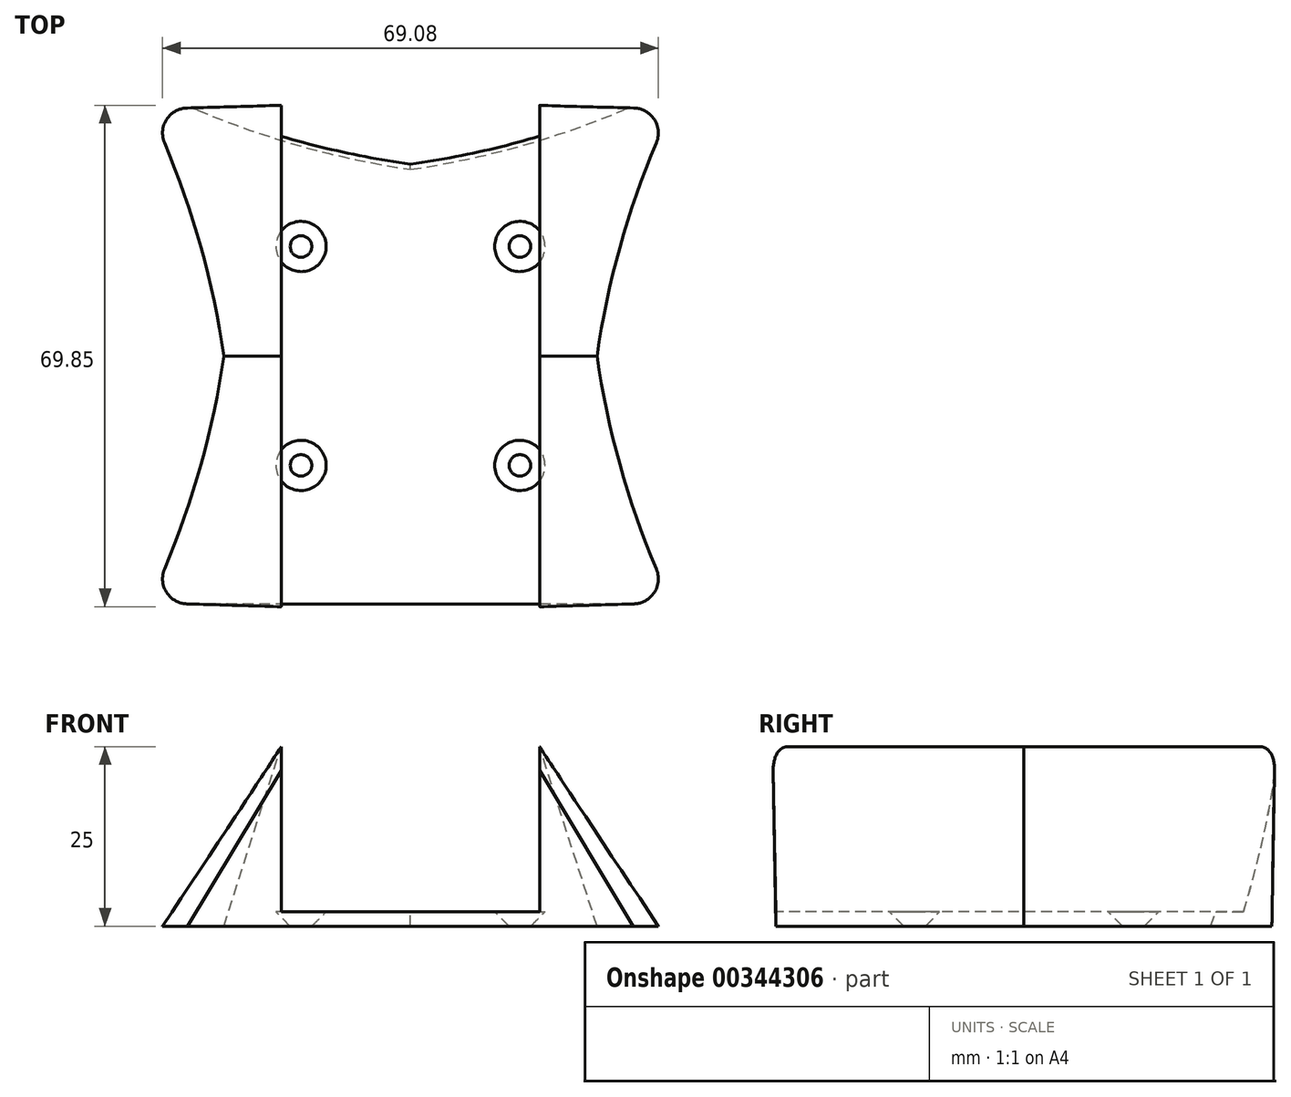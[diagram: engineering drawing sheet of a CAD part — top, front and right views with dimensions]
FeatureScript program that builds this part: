
annotation { "Feature Type Name" : "Feature", "Feature Type Description" : "" }
export const myFeature = defineFeature(function(context is Context, id is Id, definition is map)
    precondition{}
    {
        {
            var Q0;
            Q0=qCreatedBy(makeId("Top.planeOp"),FACE);
            var sketch = newSketch(context, id + "F0", { "sketchPlane" : qUnion([Q0])});
            skLineSegment(sketch, "E0", {"start": v(0, 114.28) * mm, "end": v(0, -108.92) * mm, "construction": true});
            skLineSegment(sketch, "E1", {"start": v(-111.96, 0) * mm, "end": v(120.54, 0) * mm, "construction": true});
            skLineSegment(sketch, "E2", {"start": v(0, 0) * mm, "end": v(98.63, 98.63) * mm, "construction": true});
            skLineSegment(sketch, "E3.0", {"start": v(7.81, 0.88) * mm, "end": v(15.31, 8.38) * mm, "construction": true});
            skCircle(sketch, "E4", {"center": v(15.25, 15.25) * mm, "radius": 1.5 * mm, "construction": true});
            skCircle(sketch, "E5", {"center": v(29.4, 29.4) * mm, "radius": 1.5 * mm, "construction": true});
            skPoint(sketch, "E6", {"position": v(33.52, 33.52) * mm});
            skArc(sketch, "E7", {"start": v(34.27, 29.68) * mm, "mid": v(34.48, 31.71) * mm, "end": v(33.52, 33.52) * mm});
            skLineSegment(sketch, "E8", {"start": v(34.41, 30.1) * mm, "end": v(26, 0) * mm, "construction": true});
            skArc(sketch, "E9", {"start": v(34.27, 29.68) * mm, "mid": v(29.18, 15.1) * mm, "end": v(26, 0) * mm});
            skLineSegment(sketch, "E10", {"start": v(16.13, 0) * mm, "end": v(17.43, 7.28) * mm, "construction": true});
            skArc(sketch, "E11", {"start": v(17.43, 7.28) * mm, "mid": v(16.78, 8.6) * mm, "end": v(15.31, 8.38) * mm, "construction": true});
            skLineSegment(sketch, "E12", {"start": v(18.7, 18.7) * mm, "end": v(19.74, 17.1) * mm, "construction": true});
            skArc(sketch, "E13", {"start": v(19.74, 17.1) * mm, "mid": v(20.87, 16.53) * mm, "end": v(21.92, 17.25) * mm, "construction": true});
            skArc(sketch, "E14", {"start": v(24.57, 22.9) * mm, "mid": v(24.67, 23.66) * mm, "end": v(24.32, 24.32) * mm, "construction": true});
            skLineSegment(sketch, "E15", {"start": v(21.92, 17.25) * mm, "end": v(24.57, 22.9) * mm, "construction": true});
            skArc(sketch, "E16.MirrorCS", {"start": v(29.68, 34.27) * mm, "mid": v(31.71, 34.48) * mm, "end": v(33.52, 33.52) * mm});
            skArc(sketch, "E17.MirrorCS", {"start": v(29.68, 34.27) * mm, "mid": v(15.1, 29.18) * mm, "end": v(0, 26) * mm});
            skArc(sketch, "E18.MirrorCS", {"start": v(22.9, 24.57) * mm, "mid": v(23.66, 24.67) * mm, "end": v(24.32, 24.32) * mm, "construction": true});
            skLineSegment(sketch, "E19.MirrorCS", {"start": v(17.25, 21.92) * mm, "end": v(22.9, 24.57) * mm, "construction": true});
            skArc(sketch, "E20.MirrorCS", {"start": v(17.1, 19.74) * mm, "mid": v(16.53, 20.87) * mm, "end": v(17.25, 21.92) * mm, "construction": true});
            skLineSegment(sketch, "E21.MirrorCS", {"start": v(18.7, 18.7) * mm, "end": v(17.1, 19.74) * mm, "construction": true});
            skLineSegment(sketch, "E22.MirrorCS", {"start": v(0, 16.13) * mm, "end": v(7.28, 17.43) * mm, "construction": true});
            skArc(sketch, "E23.MirrorCS", {"start": v(7.28, 17.43) * mm, "mid": v(8.6, 16.78) * mm, "end": v(8.38, 15.31) * mm, "construction": true});
            skLineSegment(sketch, "E24.MirrorCS", {"start": v(0.88, 7.81) * mm, "end": v(8.38, 15.31) * mm, "construction": true});
            skArc(sketch, "E25.MirrorCS", {"start": v(-17.1, 19.74) * mm, "mid": v(-16.53, 20.87) * mm, "end": v(-17.25, 21.92) * mm, "construction": true});
            skLineSegment(sketch, "E26.MirrorCS", {"start": v(-18.7, 18.7) * mm, "end": v(-19.74, 17.1) * mm, "construction": true});
            skArc(sketch, "E27.MirrorCS", {"start": v(-24.57, 22.9) * mm, "mid": v(-24.67, 23.66) * mm, "end": v(-24.32, 24.32) * mm, "construction": true});
            skArc(sketch, "E28.MirrorCS", {"start": v(-22.9, 24.57) * mm, "mid": v(-23.66, 24.67) * mm, "end": v(-24.32, 24.32) * mm, "construction": true});
            skLineSegment(sketch, "E29.MirrorCS", {"start": v(-18.7, 18.7) * mm, "end": v(-17.1, 19.74) * mm, "construction": true});
            skArc(sketch, "E30.MirrorCS", {"start": v(-19.74, 17.1) * mm, "mid": v(-20.87, 16.53) * mm, "end": v(-21.92, 17.25) * mm, "construction": true});
            skArc(sketch, "E31.MirrorCS", {"start": v(-7.28, 17.43) * mm, "mid": v(-8.6, 16.78) * mm, "end": v(-8.38, 15.31) * mm, "construction": true});
            skLineSegment(sketch, "E32.MirrorCS", {"start": v(-21.92, 17.25) * mm, "end": v(-24.57, 22.9) * mm, "construction": true});
            skArc(sketch, "E33.MirrorCS", {"start": v(-29.68, 34.27) * mm, "mid": v(-15.1, 29.18) * mm, "end": v(0, 26) * mm});
            skLineSegment(sketch, "E34.MirrorCS", {"start": v(-17.25, 21.92) * mm, "end": v(-22.9, 24.57) * mm, "construction": true});
            skLineSegment(sketch, "E35.MirrorCS", {"start": v(0, 16.13) * mm, "end": v(-7.28, 17.43) * mm, "construction": true});
            skArc(sketch, "E36.MirrorCS", {"start": v(-17.43, 7.28) * mm, "mid": v(-16.78, 8.6) * mm, "end": v(-15.31, 8.38) * mm, "construction": true});
            skLineSegment(sketch, "E37.MirrorCS", {"start": v(-16.13, 0) * mm, "end": v(-17.43, 7.28) * mm, "construction": true});
            skArc(sketch, "E38.MirrorCS", {"start": v(-34.27, 29.68) * mm, "mid": v(-29.18, 15.1) * mm, "end": v(-26, 0) * mm});
            skLineSegment(sketch, "E39.MirrorCS", {"start": v(-0.88, 7.81) * mm, "end": v(-8.38, 15.31) * mm, "construction": true});
            skArc(sketch, "E40.MirrorCS", {"start": v(-34.27, 29.68) * mm, "mid": v(-34.48, 31.71) * mm, "end": v(-33.52, 33.52) * mm});
            skArc(sketch, "E41.MirrorCS", {"start": v(-29.68, 34.27) * mm, "mid": v(-31.71, 34.48) * mm, "end": v(-33.52, 33.52) * mm});
            skCircle(sketch, "E42.MirrorC", {"center": v(-29.4, 29.4) * mm, "radius": 1.5 * mm, "construction": true});
            skLineSegment(sketch, "E43.MirrorCS", {"start": v(-7.81, 0.88) * mm, "end": v(-15.31, 8.38) * mm, "construction": true});
            skCircle(sketch, "E44.MirrorC", {"center": v(-15.25, 15.25) * mm, "radius": 1.5 * mm, "construction": true});
            skPoint(sketch, "E45.MirrorP", {"position": v(-33.52, 33.52) * mm});
            skArc(sketch, "E46.MirrorCS", {"start": v(24.57, -22.9) * mm, "mid": v(24.67, -23.66) * mm, "end": v(24.32, -24.32) * mm, "construction": true});
            skArc(sketch, "E47.MirrorCS", {"start": v(22.9, -24.57) * mm, "mid": v(23.66, -24.67) * mm, "end": v(24.32, -24.32) * mm, "construction": true});
            skArc(sketch, "E48.MirrorCS", {"start": v(-24.57, -22.9) * mm, "mid": v(-24.67, -23.66) * mm, "end": v(-24.32, -24.32) * mm, "construction": true});
            skArc(sketch, "E49.MirrorCS", {"start": v(17.1, -19.74) * mm, "mid": v(16.53, -20.87) * mm, "end": v(17.25, -21.92) * mm, "construction": true});
            skArc(sketch, "E50.MirrorCS", {"start": v(-17.43, -7.28) * mm, "mid": v(-16.78, -8.6) * mm, "end": v(-15.31, -8.38) * mm, "construction": true});
            skArc(sketch, "E51.MirrorCS", {"start": v(29.68, -34.27) * mm, "mid": v(30.35, -34.47) * mm, "end": v(31.04, -34.54) * mm, "construction": true});
            skArc(sketch, "E52.MirrorCS", {"start": v(34.27, -29.68) * mm, "mid": v(34.48, -31.71) * mm, "end": v(33.52, -33.52) * mm});
            skArc(sketch, "E53.MirrorCS", {"start": v(17.43, -7.28) * mm, "mid": v(16.78, -8.6) * mm, "end": v(15.31, -8.38) * mm, "construction": true});
            skLineSegment(sketch, "E54.MirrorCS", {"start": v(18.7, -18.7) * mm, "end": v(19.74, -17.1) * mm, "construction": true});
            skArc(sketch, "E55.MirrorCS", {"start": v(19.74, -17.1) * mm, "mid": v(20.87, -16.53) * mm, "end": v(21.92, -17.25) * mm, "construction": true});
            skArc(sketch, "E56.MirrorCS", {"start": v(-22.9, -24.57) * mm, "mid": v(-23.66, -24.67) * mm, "end": v(-24.32, -24.32) * mm, "construction": true});
            skArc(sketch, "E57.MirrorCS", {"start": v(-34.27, -29.68) * mm, "mid": v(-34.48, -31.71) * mm, "end": v(-33.52, -33.52) * mm});
            skArc(sketch, "E58.MirrorCS", {"start": v(7.28, -17.43) * mm, "mid": v(8.6, -16.78) * mm, "end": v(8.38, -15.31) * mm, "construction": true});
            skLineSegment(sketch, "E59.MirrorCS", {"start": v(18.7, -18.7) * mm, "end": v(17.1, -19.74) * mm, "construction": true});
            skArc(sketch, "E60.MirrorCS", {"start": v(-29.68, -34.27) * mm, "mid": v(-30.35, -34.47) * mm, "end": v(-31.04, -34.54) * mm, "construction": true});
            skArc(sketch, "E61.MirrorCS", {"start": v(-19.74, -17.1) * mm, "mid": v(-20.87, -16.53) * mm, "end": v(-21.92, -17.25) * mm, "construction": true});
            skLineSegment(sketch, "E62.MirrorCS", {"start": v(-18.7, -18.7) * mm, "end": v(-17.1, -19.74) * mm, "construction": true});
            skArc(sketch, "E63.MirrorCS", {"start": v(-7.28, -17.43) * mm, "mid": v(-8.6, -16.78) * mm, "end": v(-8.38, -15.31) * mm, "construction": true});
            skLineSegment(sketch, "E64.MirrorCS", {"start": v(-18.7, -18.7) * mm, "end": v(-19.74, -17.1) * mm, "construction": true});
            skArc(sketch, "E65.MirrorCS", {"start": v(-17.1, -19.74) * mm, "mid": v(-16.53, -20.87) * mm, "end": v(-17.25, -21.92) * mm, "construction": true});
            skLineSegment(sketch, "E66.MirrorCS", {"start": v(21.92, -17.25) * mm, "end": v(24.57, -22.9) * mm, "construction": true});
            skCircle(sketch, "E67.MirrorC", {"center": v(15.25, -15.25) * mm, "radius": 1.5 * mm, "construction": true});
            skLineSegment(sketch, "E68.MirrorCS", {"start": v(-7.81, -0.88) * mm, "end": v(-15.31, -8.38) * mm, "construction": true});
            skLineSegment(sketch, "E69.MirrorCS", {"start": v(7.81, -0.88) * mm, "end": v(15.31, -8.38) * mm, "construction": true});
            skCircle(sketch, "E70.MirrorC", {"center": v(29.4, -29.4) * mm, "radius": 1.5 * mm, "construction": true});
            skArc(sketch, "E71.MirrorCS", {"start": v(34.27, -29.68) * mm, "mid": v(29.18, -15.1) * mm, "end": v(26, 0) * mm});
            skLineSegment(sketch, "E72.MirrorCS", {"start": v(16.13, 0) * mm, "end": v(17.43, -7.28) * mm, "construction": true});
            skLineSegment(sketch, "E73.MirrorCS", {"start": v(17.25, -21.92) * mm, "end": v(22.9, -24.57) * mm, "construction": true});
            skCircle(sketch, "E74.MirrorC", {"center": v(-15.25, -15.25) * mm, "radius": 1.5 * mm, "construction": true});
            skLineSegment(sketch, "E75.MirrorCS", {"start": v(-17.25, -21.92) * mm, "end": v(-22.9, -24.57) * mm, "construction": true});
            skLineSegment(sketch, "E76.MirrorCS", {"start": v(0.88, -7.81) * mm, "end": v(8.38, -15.31) * mm, "construction": true});
            skLineSegment(sketch, "E77.MirrorCS", {"start": v(-0.88, -7.81) * mm, "end": v(-8.38, -15.31) * mm, "construction": true});
            skLineSegment(sketch, "E78.MirrorCS", {"start": v(-21.92, -17.25) * mm, "end": v(-24.57, -22.9) * mm, "construction": true});
            skArc(sketch, "E79.MirrorCS", {"start": v(29.68, -34.27) * mm, "mid": v(15.1, -29.18) * mm, "end": v(0, -26) * mm, "construction": true});
            skArc(sketch, "E80.MirrorCS", {"start": v(-34.27, -29.68) * mm, "mid": v(-29.18, -15.1) * mm, "end": v(-26, 0) * mm});
            skLineSegment(sketch, "E81.MirrorCS", {"start": v(-16.13, 0) * mm, "end": v(-17.43, -7.28) * mm, "construction": true});
            skPoint(sketch, "E82.MirrorP", {"position": v(-33.52, -33.52) * mm});
            skLineSegment(sketch, "E83.MirrorCS", {"start": v(0, -16.13) * mm, "end": v(7.28, -17.43) * mm, "construction": true});
            skLineSegment(sketch, "E84.MirrorCS", {"start": v(0, -16.13) * mm, "end": v(-7.28, -17.43) * mm, "construction": true});
            skCircle(sketch, "E85.MirrorC", {"center": v(-29.4, -29.4) * mm, "radius": 1.5 * mm, "construction": true});
            skPoint(sketch, "E86.MirrorP", {"position": v(33.52, -33.52) * mm});
            skArc(sketch, "E87.MirrorCS", {"start": v(-29.68, -34.27) * mm, "mid": v(-15.1, -29.18) * mm, "end": v(0, -26) * mm, "construction": true});
            skArc(sketch, "E88", {"start": v(7.81, 0.88) * mm, "mid": v(7.45, 0) * mm, "end": v(7.81, -0.88) * mm, "construction": true});
            skArc(sketch, "E89", {"start": v(-0.88, 7.81) * mm, "mid": v(0, 7.45) * mm, "end": v(0.88, 7.81) * mm, "construction": true});
            skArc(sketch, "E90", {"start": v(-7.81, -0.88) * mm, "mid": v(-7.45, 0) * mm, "end": v(-7.81, 0.88) * mm, "construction": true});
            skArc(sketch, "E91", {"start": v(0.88, -7.81) * mm, "mid": v(0, -7.45) * mm, "end": v(-0.88, -7.81) * mm, "construction": true});
            skPoint(sketch, "E92.orphan", {"position": v(6.93, 0) * mm});
            skPoint(sketch, "E93.orphan", {"position": v(0, -6.93) * mm});
            skPoint(sketch, "E94.orphan", {"position": v(-6.93, 0) * mm});
            skPoint(sketch, "E95.orphan", {"position": v(0, 6.93) * mm});
            skLineSegment(sketch, "E96", {"start": v(31.04, -34.54) * mm, "end": v(0, -34.54) * mm});
            skArc(sketch, "E97", {"start": v(-31.04, -34.54) * mm, "mid": v(-32.38, -34.28) * mm, "end": v(-33.52, -33.52) * mm});
            skArc(sketch, "E98", {"start": v(31.04, -34.54) * mm, "mid": v(32.38, -34.28) * mm, "end": v(33.52, -33.52) * mm});
            skLineSegment(sketch, "E99", {"start": v(0, -34.54) * mm, "end": v(-31.04, -34.54) * mm});
            skSolve(sketch);
        }
        {
            var Q0;
            Q0=qCreatedBy(makeId("Top.planeOp"),FACE);
            cPlane(context, id + "F1", {"entities" : qUnion([Q0]), "cplaneType" : CPlaneType.OFFSET, "offset" : 25 * mm, "width" : 150 * mm, "height" : 150 * mm});
        }
        {
            var Q0;
            Q0=qCreatedBy(id+"F1.planeOp",FACE);
            var sketch = newSketch(context, id + "F2", { "sketchPlane" : qUnion([Q0])});
            skLineSegment(sketch, "E100.bottom", {"start": v(0, 35) * mm, "end": v(16, 35) * mm});
            skLineSegment(sketch, "E100.top", {"start": v(-16, -35) * mm, "end": v(0, -35) * mm});
            skLineSegment(sketch, "E100.left", {"start": v(-18, 33) * mm, "end": v(-18, 0) * mm});
            skLineSegment(sketch, "E100.right", {"start": v(18, 0) * mm, "end": v(18, -33) * mm});
            skLineSegment(sketch, "E101", {"start": v(-18, 35) * mm, "end": v(18, -35) * mm, "construction": true});
            skPoint(sketch, "E102.visualSharp", {"position": v(-18, 35) * mm});
            skArc(sketch, "E102.filletArc", {"start": v(-16, 35) * mm, "mid": v(-16.6, 34.9) * mm, "end": v(-17.13, 34.65) * mm});
            skPoint(sketch, "E103.visualSharp", {"position": v(18, 35) * mm});
            skArc(sketch, "E103.filletArc", {"start": v(18, 33) * mm, "mid": v(17.85, 33.77) * mm, "end": v(17.41, 34.41) * mm});
            skPoint(sketch, "E104.visualSharp", {"position": v(18, -35) * mm});
            skArc(sketch, "E104.filletArc", {"start": v(16, -35) * mm, "mid": v(16.77, -34.85) * mm, "end": v(17.41, -34.41) * mm});
            skPoint(sketch, "E105.visualSharp", {"position": v(-18, -35) * mm});
            skArc(sketch, "E105.filletArc", {"start": v(-18, -33) * mm, "mid": v(-17.85, -33.77) * mm, "end": v(-17.41, -34.41) * mm});
            skPoint(sketch, "E106", {"position": v(0, -35) * mm});
            skPoint(sketch, "E107", {"position": v(0, 35) * mm});
            skLineSegment(sketch, "E108", {"start": v(0, -35) * mm, "end": v(16, -35) * mm});
            skLineSegment(sketch, "E109", {"start": v(18, 0) * mm, "end": v(18, 33) * mm});
            skLineSegment(sketch, "E110", {"start": v(0, 35) * mm, "end": v(-16, 35) * mm});
            skLineSegment(sketch, "E111", {"start": v(-18, -33) * mm, "end": v(-18, 0) * mm});
            skLineSegment(sketch, "E112", {"start": v(-18, 35) * mm, "end": v(-16, 33) * mm, "construction": true});
            skLineSegment(sketch, "E113", {"start": v(16, 33) * mm, "end": v(18, 35) * mm, "construction": true});
            skLineSegment(sketch, "E114", {"start": v(16, -33) * mm, "end": v(18, -35) * mm, "construction": true});
            skLineSegment(sketch, "E115", {"start": v(-16, -33) * mm, "end": v(-18, -35) * mm, "construction": true});
            skArc(sketch, "E116", {"start": v(-17.41, -34.41) * mm, "mid": v(-16.77, -34.85) * mm, "end": v(-16, -35) * mm});
            skArc(sketch, "E117", {"start": v(-17.13, 34.65) * mm, "mid": v(-17.77, 33.93) * mm, "end": v(-18, 33) * mm});
            skArc(sketch, "E118", {"start": v(17.41, 34.41) * mm, "mid": v(16.77, 34.85) * mm, "end": v(16, 35) * mm});
            skArc(sketch, "E119", {"start": v(17.41, -34.41) * mm, "mid": v(17.85, -33.77) * mm, "end": v(18, -33) * mm});
            skSolve(sketch);
        }
        {
            var Q0;
            Q0=qCreatedBy(makeId("Front.planeOp"),FACE);
            var sketch = newSketch(context, id + "F3", { "sketchPlane" : qUnion([Q0])});
            skLineSegment(sketch, "E120", {"start": v(0, 0) * mm, "end": v(0, 70.76) * mm, "construction": true});
            skSolve(sketch);
        }
        {
            var Q0;
            Q0 = qSketchRegion(id + "F0", true);
            var Q1;
            Q1 = qSketchRegion(id + "F2", true);
            loft(context, id + "F4", {"sheetProfilesArray" : [{ "sheetProfileEntities" : qUnion([Q0]) }, { "sheetProfileEntities" : qUnion([Q1]) }]});
        }
        {
            var Q0;
            Q0=qCreatedBy(makeId("Front.planeOp"),FACE);
            var sketch = newSketch(context, id + "F5", { "sketchPlane" : qUnion([Q0])});
            skLineSegment(sketch, "E121", {"start": v(0, 0) * mm, "end": v(0, 36.29) * mm, "construction": true});
            skLineSegment(sketch, "E122.0", {"start": v(-16, 25) * mm, "end": v(16, 25) * mm});
            skLineSegment(sketch, "E123", {"start": v(18, 25) * mm, "end": v(18, 2) * mm});
            skLineSegment(sketch, "E124", {"start": v(18, 2) * mm, "end": v(0, 2) * mm});
            skLineSegment(sketch, "E125", {"start": v(16, 25) * mm, "end": v(18, 25) * mm});
            skLineSegment(sketch, "E126.MirrorCS", {"start": v(-18, 2) * mm, "end": v(0, 2) * mm});
            skLineSegment(sketch, "E127.MirrorCS", {"start": v(-16, 25) * mm, "end": v(-18, 25) * mm});
            skLineSegment(sketch, "E128.MirrorCS", {"start": v(-18, 25) * mm, "end": v(-18, 2) * mm});
            skSolve(sketch);
        }
        {
            var Q0;
            Q0 = qSketchRegion(id + "F5", true);
            extrude(context, id + "F6", {"entities" : qUnion([Q0]), "operationType" : NewBodyOperationType.REMOVE, "endBound" : BoundingType.THROUGH_ALL, "oppositeDirection" : true, "depth" : 25 * mm, "hasSecondDirection" : true, "secondDirectionBound" : SecondDirectionBoundingType.THROUGH_ALL, "secondDirectionOppositeDirection" : false, "secondDirectionDepth" : 25 * mm});
        }
        {
            var Q0;
            Q0=qCreatedBy(makeId("Top.planeOp"),FACE);
            var sketch = newSketch(context, id + "F7", { "sketchPlane" : qUnion([Q0])});
            skLineSegment(sketch, "E129", {"start": v(-15.25, 15.25) * mm, "end": v(15.25, -15.25) * mm, "construction": true});
            skLineSegment(sketch, "E130", {"start": v(15.25, 15.25) * mm, "end": v(-15.25, -15.25) * mm, "construction": true});
            skCircle(sketch, "E131", {"center": v(-15.25, 15.25) * mm, "radius": 1.5 * mm});
            skCircle(sketch, "E132", {"center": v(15.25, 15.25) * mm, "radius": 1.5 * mm});
            skCircle(sketch, "E133", {"center": v(-15.25, -15.25) * mm, "radius": 1.5 * mm});
            skCircle(sketch, "E134", {"center": v(15.25, -15.25) * mm, "radius": 1.5 * mm});
            skSolve(sketch);
        }
        {
            var Q0;
            Q0 = qSketchRegion(id + "F7", true);
            extrude(context, id + "F8", {"entities" : qUnion([Q0]), "operationType" : NewBodyOperationType.REMOVE, "depth" : 2 * mm, "hasDraft" : true, "draftAngle" : 45 * degree});
        }
    });
